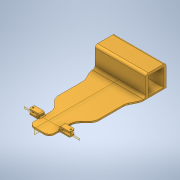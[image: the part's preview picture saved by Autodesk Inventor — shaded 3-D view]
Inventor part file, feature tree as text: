
AUTODESK INVENTOR PART (.ipt)
format: ipt  version: 2020 (Build 240168000, 168)  size: 317,952 bytes
history: native  units: mm
features: fillet x14, sketch x4, extrude x3, plane x2, hole x1, mirror x1
ambient origin geometry x8: Origin, YZ Plane, XZ Plane, XY Plane, X Axis, Y Axis, Z Axis, Center Point
bodies: Body1 (feature_tree)
feature tree (25):
  extrude  "Extrusion2"  Depth=60.0mm
  plane  "Work Plane1"
  extrude  "Extrusion3"  Depth=40.0mm
  fillet  "Fillet1"  Radius=50.0mm
  fillet  "Fillet2"  Radius=50.0mm
  fillet  "Fillet3"  Radius=20.0mm
  fillet  "Fillet4"  Radius=20.0mm
  fillet  "Fillet5"  Radius=40.0mm
  hole  "Hole1"  [1 undecoded]
  plane  "Work Plane2"
  mirror  "Mirror1"
  fillet  "Fillet6"  Radius=10.0mm
  fillet  "Fillet7"  Radius=20.0mm
  fillet  "Fillet8"  Radius=200.0mm
  fillet  "Fillet9"  Radius=20.0mm
  fillet  "Fillet10"  Radius=10.0mm
  fillet  "Fillet11"  Radius=3.0mm
  extrude  "Extrusion4"  Depth=5.0mm
  fillet  "Fillet12"  Radius=2.5mm
  fillet  "Fillet13"  Radius=2.5mm
  fillet  "Fillet14"  Radius=20.0mm
  sketch  "Sketch1"  dims[d23=50.0mm d24=60.0mm]
  sketch  "Sketch4"  dims[d25=60.0mm d26=50.0mm d27=50.0mm d28=50.0mm d29=20.0mm d30=20.0mm d31=40.0mm]
  sketch  "Sketch5"  dims[d32=100.0mm d34=10.0mm d35=10.0mm d36=20.0mm d37=200.0mm d38=20.0mm d39=10.0mm d40=3.0mm d41=0.0mm]
  sketch  "Sketch6"  dims[d42=-25.0mm d61=15.0mm d66=5.0mm d67=2.5mm d68=2.5mm d69=20.0mm d70=15.0mm d71=2.0mm d72=10.0mm d73=0.0mm d74=2.0mm d75=2.0mm d76=0.5mm d77=1.26mm d78=0.5mm d79=3.0mm d80=6.0mm d81=4.0mm d82=2.0mm d83=90.0deg d84=8.0mm d85=20.594885mm d86=3.0mm d87=5.0mm d88=50.0mm d89=2.0mm d90=2.12mm d91=1.0mm d92=2.46mm d93=1.0mm d94=2.0mm d95=40.0mm d96=40.0mm d97=5.0mm d98=5.0mm d100=5.0mm d101=100.0mm d102=0.0mm d103=5.0mm d104=5.0mm d105=5.0mm d57=0.5mm d58=0.872665mm d59=0.5mm d60=0.872665mm]
note: 1 required parameter value undecoded (feature->parameter linkage not recoverable at this tier; creation-order binding heuristic only, values carry confidence <= 0.55)
